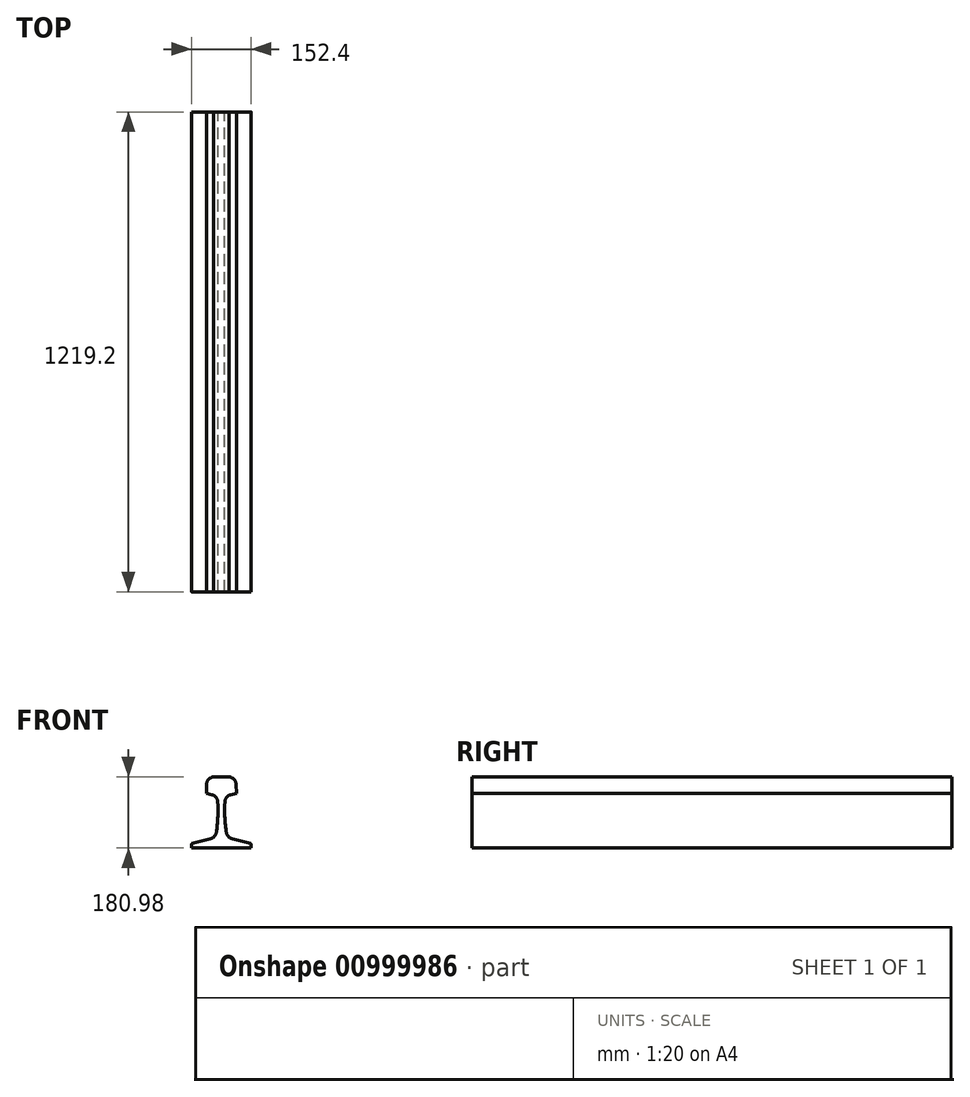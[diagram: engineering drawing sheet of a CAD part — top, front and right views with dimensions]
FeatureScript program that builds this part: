
annotation { "Feature Type Name" : "Feature", "Feature Type Description" : "" }
export const myFeature = defineFeature(function(context is Context, id is Id, definition is map)
    precondition{}
    {
        {
            var Q0;
            Q0=qCreatedBy(makeId("Front.planeOp"),FACE);
            var sketch = newSketch(context, id + "F0", { "sketchPlane" : qUnion([Q0])});
            skLineSegment(sketch, "E0", {"start": v(-76.2, 0) * mm, "end": v(76.2, 0) * mm});
            skLineSegment(sketch, "E1", {"start": v(0, 30.16) * mm, "end": v(-76.2, 10.88) * mm});
            skLineSegment(sketch, "E2", {"start": v(0, 30.16) * mm, "end": v(76.2, 10.88) * mm});
            skLineSegment(sketch, "E3", {"start": v(0, 30.16) * mm, "end": v(-76.4, 30.16) * mm, "construction": true});
            skLineSegment(sketch, "E4", {"start": v(-76.2, 0) * mm, "end": v(-76.2, 10.88) * mm});
            skLineSegment(sketch, "E5", {"start": v(76.2, 0) * mm, "end": v(76.2, 10.88) * mm});
            skLineSegment(sketch, "E6.bottom", {"start": v(8.33, 28.05) * mm, "end": v(-8.33, 28.05) * mm});
            skLineSegment(sketch, "E6.top", {"start": v(8.33, 131.5) * mm, "end": v(-8.33, 131.5) * mm});
            skLineSegment(sketch, "E6.left", {"start": v(8.33, 28.05) * mm, "end": v(8.33, 131.5) * mm});
            skLineSegment(sketch, "E6.right", {"start": v(-8.33, 28.05) * mm, "end": v(-8.33, 131.5) * mm});
            skPoint(sketch, "E6.middle", {"position": v(0, 79.77) * mm});
            skCircle(sketch, "E7", {"center": v(-414.73, 98.43) * mm, "radius": 406.4 * mm, "construction": true});
            skCircle(sketch, "E8", {"center": v(-211.53, 98.43) * mm, "radius": 203.2 * mm, "construction": true});
            skPoint(sketch, "E9", {"position": v(-14.76, 26.43) * mm});
            skPoint(sketch, "E10", {"position": v(-8.33, 98.42) * mm});
            skPoint(sketch, "E11", {"position": v(-14.1, 30.16) * mm});
            skArc(sketch, "E12", {"start": v(-14.76, 26.43) * mm, "mid": v(-9.94, 62.28) * mm, "end": v(-8.33, 98.42) * mm});
            skLineSegment(sketch, "E13", {"start": v(0, 129.38) * mm, "end": v(-38.1, 139.02) * mm});
            skLineSegment(sketch, "E14", {"start": v(0, 129.38) * mm, "end": v(-83.84, 129.38) * mm, "construction": true});
            skLineSegment(sketch, "E15", {"start": v(0, 129.38) * mm, "end": v(38.1, 139.02) * mm});
            skLineSegment(sketch, "E16.top", {"start": v(-38.1, 139.02) * mm, "end": v(38.1, 139.02) * mm});
            skLineSegment(sketch, "E16.left", {"start": v(-38.1, 180.98) * mm, "end": v(-38.1, 139.02) * mm, "construction": true});
            skLineSegment(sketch, "E16.right", {"start": v(38.1, 180.98) * mm, "end": v(38.1, 139.02) * mm, "construction": true});
            skPoint(sketch, "E17", {"position": v(-11.16, 132.2) * mm});
            skPoint(sketch, "E18", {"position": v(-10.7, 129.38) * mm});
            skArc(sketch, "E19", {"start": v(-8.33, 98.42) * mm, "mid": v(-9.04, 115.37) * mm, "end": v(-11.16, 132.2) * mm});
            skLineSegment(sketch, "E20", {"start": v(-38.1, 139.02) * mm, "end": v(-37.6, 161.4) * mm});
            skLineSegment(sketch, "E21", {"start": v(38.1, 139.02) * mm, "end": v(37.6, 161.4) * mm});
            skCircle(sketch, "E22", {"center": v(211.53, 98.43) * mm, "radius": 203.2 * mm, "construction": true});
            skCircle(sketch, "E23", {"center": v(414.73, 98.43) * mm, "radius": 406.4 * mm, "construction": true});
            skPoint(sketch, "E24", {"position": v(14.76, 26.43) * mm});
            skPoint(sketch, "E25", {"position": v(8.33, 98.43) * mm});
            skPoint(sketch, "E26", {"position": v(11.16, 132.2) * mm});
            skPoint(sketch, "E27", {"position": v(14.1, 30.16) * mm});
            skArc(sketch, "E28", {"start": v(8.33, 98.42) * mm, "mid": v(9.94, 62.28) * mm, "end": v(14.76, 26.43) * mm});
            skLineSegment(sketch, "E29", {"start": v(0, 30.16) * mm, "end": v(75.97, 30.16) * mm, "construction": true});
            skLineSegment(sketch, "E30", {"start": v(0, 129.38) * mm, "end": v(82.6, 129.38) * mm, "construction": true});
            skPoint(sketch, "E31", {"position": v(10.7, 129.38) * mm});
            skArc(sketch, "E32", {"start": v(11.16, 132.2) * mm, "mid": v(9.04, 115.37) * mm, "end": v(8.33, 98.43) * mm});
            skLineSegment(sketch, "E33", {"start": v(-19.05, 180.98) * mm, "end": v(19.05, 180.98) * mm});
            skCircle(sketch, "E34", {"center": v(0, -72.3) * mm, "radius": 254 * mm, "construction": true});
            skPoint(sketch, "E35", {"position": v(0, 181.7) * mm});
            skArc(sketch, "E36", {"start": v(19.05, 180.97) * mm, "mid": v(0, 181.7) * mm, "end": v(-19.05, 180.97) * mm});
            skCircle(sketch, "E37", {"center": v(17.54, 160.96) * mm, "radius": 20.07 * mm, "construction": true});
            skCircle(sketch, "E38", {"center": v(-17.54, 160.96) * mm, "radius": 20.07 * mm, "construction": true});
            skArc(sketch, "E39", {"start": v(-19.05, 180.98) * mm, "mid": v(-32.1, 174.77) * mm, "end": v(-37.6, 161.4) * mm});
            skArc(sketch, "E40", {"start": v(37.6, 161.4) * mm, "mid": v(32.1, 174.77) * mm, "end": v(19.05, 180.98) * mm});
            skSolve(sketch);
        }
        {
            var Q0;
            Q0=makeQuery(id+"F0.imprint","IMPRINT",FACE,{"disambiguationData":[TD([[makeQuery(id+"F0.imprint","IMPRINT",EDGE,{"derivedFrom":sQuery(id+"F0.wireOp",EDGE,"E0")}),1.0]])]});
            var Q1;
            {var subQ3=sQuery(id+"F0.wireOp",EDGE,"E12");Q1=makeQuery(id+"F0.imprint","IMPRINT",FACE,{"disambiguationData":[TD([[makeQuery(id+"F0.imprint","IMPRINT",EDGE,{"derivedFrom":subQ3}),-1.0]])]});}
            var Q2;
            {var subQ3=sQuery(id+"F0.wireOp",EDGE,"E28");Q2=makeQuery(id+"F0.imprint","IMPRINT",FACE,{"disambiguationData":[TD([[makeQuery(id+"F0.imprint","IMPRINT",EDGE,{"derivedFrom":subQ3}),-1.0]])]});}
            var Q3;
            {var subQ5=sQuery(id+"F0.wireOp",EDGE,"E2");var subQ6=sQuery(id+"F0.wireOp",EDGE,"E1");var subQ7=makeQuery(id+"F0.imprint","INTERSECT",VERTEX,{"derivedFrom":[subQ6,subQ5]});Q3=makeQuery(id+"F0.imprint","IMPRINT",FACE,{"disambiguationData":[TD([[makeQuery(id+"F0.imprint","IMPRINT",EDGE,{"disambiguationData":[TD([[subQ7,-1.0]])],"derivedFrom":subQ6}),-1.0]])]});}
            var Q4;
            {var subQ3=sQuery(id+"F0.wireOp",EDGE,"E6.top");Q4=makeQuery(id+"F0.imprint","IMPRINT",FACE,{"disambiguationData":[TD([[makeQuery(id+"F0.imprint","IMPRINT",EDGE,{"derivedFrom":subQ3}),-1.0]])]});}
            var Q5;
            Q5=makeQuery(id+"F0.imprint","IMPRINT",FACE,{"disambiguationData":[TD([[makeQuery(id+"F0.imprint","IMPRINT",EDGE,{"derivedFrom":sQuery(id+"F0.wireOp",EDGE,"E16.top")}),1.0]])]});
            var Q6;
            {var subQ0=sQuery(id+"F0.wireOp",EDGE,"E6.top");Q6=makeQuery(id+"F0.imprint","IMPRINT",FACE,{"disambiguationData":[TD([[makeQuery(id+"F0.imprint","IMPRINT",EDGE,{"derivedFrom":subQ0}),1.0]])]});}
            var Q7;
            {var subQ3=sQuery(id+"F0.wireOp",EDGE,"E32");Q7=makeQuery(id+"F0.imprint","IMPRINT",FACE,{"disambiguationData":[TD([[makeQuery(id+"F0.imprint","IMPRINT",EDGE,{"derivedFrom":subQ3}),-1.0]])]});}
            var Q8;
            {var subQ3=sQuery(id+"F0.wireOp",EDGE,"E19");Q8=makeQuery(id+"F0.imprint","IMPRINT",FACE,{"disambiguationData":[TD([[makeQuery(id+"F0.imprint","IMPRINT",EDGE,{"derivedFrom":subQ3}),-1.0]])]});}
            var Q9;
            {var subQ3=sQuery(id+"F0.wireOp",EDGE,"E6.bottom");Q9=makeQuery(id+"F0.imprint","IMPRINT",FACE,{"disambiguationData":[TD([[makeQuery(id+"F0.imprint","IMPRINT",EDGE,{"derivedFrom":subQ3}),-1.0]])]});}
            extrude(context, id + "F1", {"entities" : qUnion([Q0, Q1, Q2, Q3, Q4, Q5, Q6, Q7, Q8, Q9]), "depth" : 1219.2 * mm, "offsetDistance" : 25.4 * mm});
        }
        {
            var Q0;
            Q0=makeQuery(id+"F1.opExtrude","SWEPT_EDGE",EDGE,{"disambiguationData":[OSD([sQuery(id+"F0.wireOp",EDGE,"E2"),sQuery(id+"F0.wireOp",EDGE,"E5")])]});
            var Q1;
            Q1=makeQuery(id+"F1.opExtrude","SWEPT_EDGE",EDGE,{"disambiguationData":[OSD([sQuery(id+"F0.wireOp",EDGE,"E1"),sQuery(id+"F0.wireOp",EDGE,"E4")])]});
            fillet(context, id + "F2", {"entities" : qUnion([Q0, Q1]), "radius" : 3.17 * mm, "tangentPropagation" : true, "allowEdgeOverflow" : false});
        }
        {
            var Q0;
            Q0=makeQuery(id+"F1.opExtrude","SWEPT_EDGE",EDGE,{"disambiguationData":[OSD([sQuery(id+"F0.wireOp",EDGE,"E2"),sQuery(id+"F0.wireOp",EDGE,"E28")])]});
            var Q1;
            Q1=makeQuery(id+"F1.opExtrude","SWEPT_EDGE",EDGE,{"disambiguationData":[OSD([sQuery(id+"F0.wireOp",EDGE,"E1"),sQuery(id+"F0.wireOp",EDGE,"E12")])]});
            fillet(context, id + "F3", {"entities" : qUnion([Q0, Q1]), "radius" : 22.22 * mm, "tangentPropagation" : true, "allowEdgeOverflow" : false});
        }
        {
            var Q0;
            Q0=makeQuery(id+"F1.opExtrude","SWEPT_EDGE",EDGE,{"disambiguationData":[OSD([sQuery(id+"F0.wireOp",EDGE,"E13"),sQuery(id+"F0.wireOp",EDGE,"E19")])]});
            var Q1;
            Q1=makeQuery(id+"F1.opExtrude","SWEPT_EDGE",EDGE,{"disambiguationData":[OSD([sQuery(id+"F0.wireOp",EDGE,"E15"),sQuery(id+"F0.wireOp",EDGE,"E32")])]});
            fillet(context, id + "F4", {"entities" : qUnion([Q0, Q1]), "radius" : 19.05 * mm, "tangentPropagation" : true, "allowEdgeOverflow" : false});
        }
    });
